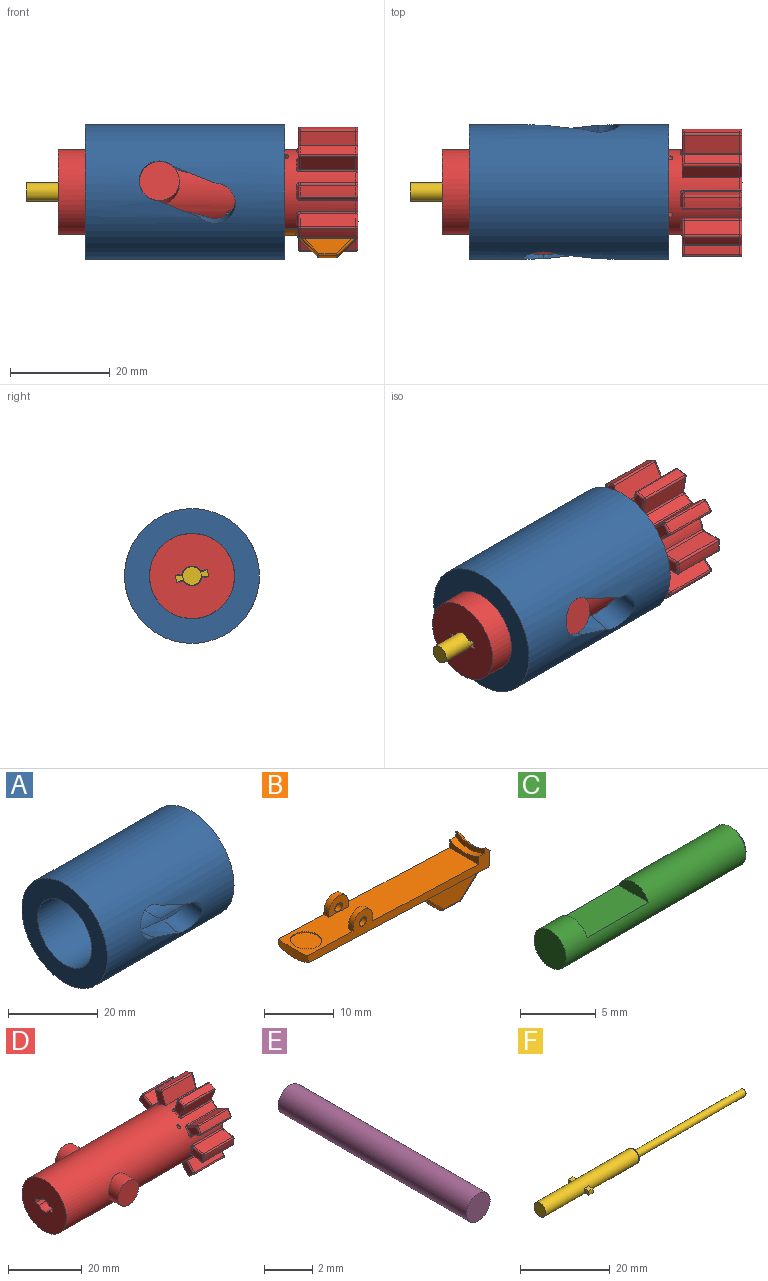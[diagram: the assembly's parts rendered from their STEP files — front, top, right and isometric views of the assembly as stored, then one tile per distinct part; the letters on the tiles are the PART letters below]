
ASSEMBLY  parts=6 mates=5
PART A: 23 faces, bbox 40x44.8x27 mm
  f0: cylinder r=8.55mm len=40mm, axis (-1,0,0), area 1773.2mm2, adj f2,f3,f5,f7,f8,f9,f10,f11
  f1: cylinder r=13.5mm len=40mm, axis (-1,0,0), area 3101mm2, adj f2,f4,f5,f7,f8,f9,f10,f12
  f2: bspline ~15.74x11.11mm, area 48.5mm2, adj f0,f1,f3,f6,f18,f19
  f3: bspline ~11.11x10.63mm, area 0mm2, adj f0,f2,f6,f18
  f4: bspline ~15.67x11.11mm, area 0mm2, adj f1,f18
  f5: bspline ~9.14x6.57mm, area 48.5mm2, adj f0,f1,f18,f19
  f6: plane 2.63x0.46mm, normal (1,0,0), area 0mm2, adj f2,f3,f18
  f7: bspline ~9.3x6.59mm, area 49.3mm2, adj f0,f1,f16,f17
  f8: plane 5.28x0.98mm, normal (1,0,0), area 0.3mm2, adj f0,f1,f11,f12,f15
  f9: plane 27.04x27.04mm, normal (1,0,0), area 339.9mm2, adj f0,f1,f20,f21,f22
  f10: plane 27x27mm, normal (-1,0,0), area 342.9mm2, adj f0,f1
  f11: bspline ~0.48x0.16mm, area 0mm2, adj f0,f8,f12
  f12: bspline ~15.74x11.11mm, area 48.5mm2, adj f0,f1,f8,f11,f17
  f13: bspline ~15.67x11.11mm, area 0.7mm2, adj f0,f1,f14,f16
  f14: plane 5.29x0.95mm, normal (1,0,0), area 0.2mm2, adj f0,f1,f13,f15
  f15: cylinder r=4.05mm len=8.96mm, axis (0,0.99,-0.17), area 65.1mm2, adj f0,f1,f8,f14
  f16: cylinder r=4.05mm len=5.76mm, axis (0,0.99,-0.17), area 12.6mm2, adj f0,f1,f7,f13
  f17: cylinder r=4.1mm len=9.08mm, axis (0,-0.98,-0.17), area 80.3mm2, adj f0,f1,f7,f12
  f18: cylinder r=4.1mm len=9.1mm, axis (0,-0.99,0.17), area 80.3mm2, adj f0,f1,f2,f3,f4,f5,f6
  f19: cylinder r=4.1mm len=9.06mm, axis (0,-0.98,-0.17), area 83.6mm2, adj f0,f1,f2,f5
  f20: plane 12.69x0.49mm, normal (0,1,0), area 3.1mm2, adj f0,f9,f22
  f21: plane 12.69x0.49mm, normal (0,-1,0), area 3.1mm2, adj f0,f9,f22
  f22: cylinder r=8.6mm len=12.71mm, axis (1,0,-0.04), area 79.2mm2, adj f0,f9,f20,f21
PART B: 61 faces, bbox 38.6x8.2x11.3 mm
  f0: plane 37.16x5.21mm, normal (0,-1,0), area 61.9mm2, adj f6,f7,f9,f10,f11,f12,f13,f15
  f1: plane 37.16x5.21mm, normal (0,1,0), area 61.9mm2, adj f4,f5,f6,f7,f10,f11,f12,f13
  f2: plane 4.03x2.88mm, normal (0,-1,0), area 7.7mm2, adj f4,f5,f7,f57,f59
  f3: plane 4.03x2.88mm, normal (0,1,0), area 7.7mm2, adj f7,f52,f53,f56,f58
  f4: plane 0.94x0.8mm, normal (1,0,-0.04), area 0.8mm2, adj f1,f2,f7,f57
  f5: plane 0.94x0.8mm, normal (-1,0,0.04), area 0.8mm2, adj f1,f2,f7,f57
  f6: cylinder r=8.5mm len=36.34mm, axis (1,0,-0.04), area 176.3mm2, adj f0,f1,f9,f17,f22,f23,f26,f27
  f7: plane 36.25x7.2mm, normal (0.04,0,1), area 182.6mm2, adj f0,f1,f2,f3,f4,f5,f51,f52
  f8: plane 11.19x4.13mm, normal (0,1,0), area 28.5mm2, adj f19,f20,f21,f22,f40,f49
  f9: torus R=8.1mm, axis (1,0,-0.04), area 0.8mm2, adj f0,f6,f15,f30
  f10: cone r=5.23mm half-angle=38.1deg, axis (1,0,-0.04), area 7.8mm2, adj f0,f1,f12,f15
  f11: plane 5.9x1.61mm, normal (-1,0,0.04), area 4.4mm2, adj f0,f1,f12,f13
  f12: torus R=5.29mm, axis (1,0,-0.04), area 0.9mm2, adj f0,f1,f10,f11
  f13: cylinder r=6mm len=5.9mm, axis (1,0,-0.04), area 7.2mm2, adj f0,f1,f11,f51
  f14: cylinder r=13mm len=3.55mm, axis (-1,0,0.04), area 7.9mm2, adj f20,f24,f41,f48
  f15: plane 5.91x3.51mm, normal (1,0,-0.04), area 14.4mm2, adj f0,f1,f9,f10,f17,f18,f19,f28
  f16: plane 11.19x4.13mm, normal (0,-1,0), area 28.5mm2, adj f24,f25,f28,f29,f37,f44
  f17: torus R=8.1mm, axis (1,0,-0.04), area 0.8mm2, adj f1,f6,f15,f18
  f18: torus R=0.8mm, axis (1,0,-0.04), area 0.5mm2, adj f15,f17,f19,f22
  f19: cylinder r=0.4mm len=0.4mm, axis (0.04,0,1), area 0mm2, adj f8,f15,f18,f47
  f20: cylinder r=0.4mm len=3.56mm, axis (-1,0,0.04), area 2.1mm2, adj f8,f14,f42,f50
  f21: cylinder r=0.4mm len=0.22mm, axis (-0.04,0,-1), area 0mm2, adj f8,f23,f38
  f22: cylinder r=0.4mm len=11.21mm, axis (1,0,-0.04), area 6.1mm2, adj f6,f8,f18,f23
  f23: bspline ~0.98x0.89mm, area 0.5mm2, adj f6,f21,f22,f26,f36
  f24: cylinder r=0.4mm len=3.56mm, axis (-1,0,0.04), area 2.1mm2, adj f14,f16,f39,f46
  f25: cylinder r=0.4mm len=0.22mm, axis (0.04,0,1), area 0mm2, adj f16,f27,f35
  f26: torus R=8.9mm, axis (1,0,-0.04), area 1.1mm2, adj f6,f23,f27,f34
  f27: bspline ~0.95x0.94mm, area 0.5mm2, adj f6,f25,f26,f29,f33
  f28: cylinder r=0.4mm len=0.4mm, axis (-0.04,0,-1), area 0mm2, adj f15,f16,f30,f43
  f29: cylinder r=0.4mm len=11.21mm, axis (1,0,-0.04), area 6.1mm2, adj f6,f16,f27,f30
  f30: torus R=0.8mm, axis (1,0,-0.04), area 0.5mm2, adj f9,f15,f28,f29
  f31: plane 4.02x3.72mm, normal (0.68,0,-0.73), area 11.7mm2, adj f44,f45,f48,f49
  f32: plane 4.04x3.74mm, normal (-0.73,0,-0.68), area 11.8mm2, adj f33,f34,f36,f37,f40,f41
  f33: bspline ~0.35x0.28mm, area 0.1mm2, adj f27,f32,f34,f35
  f34: bspline ~4.26x0.33mm, area 0.5mm2, adj f26,f32,f33,f36
  f35: sphere r=0.4mm, area 0.1mm2, adj f25,f33,f37
  f36: bspline ~0.37x0.28mm, area 0.1mm2, adj f23,f32,f34,f38
  f37: cylinder r=0.4mm len=4.24mm, axis (0.68,0,-0.73), area 3.4mm2, adj f16,f32,f35,f39
  f38: sphere r=0.4mm, area 0.1mm2, adj f21,f36,f40
  f39: sphere r=0.4mm, area 0.1mm2, adj f24,f37,f41
  f40: cylinder r=0.4mm len=4.24mm, axis (0.68,0,-0.73), area 3.4mm2, adj f8,f32,f38,f42
  f41: bspline ~2.22x0.32mm, area 0.7mm2, adj f14,f32,f39,f42
  f42: sphere r=0.4mm, area 0.1mm2, adj f20,f40,f41
  f43: sphere r=0.4mm, area 0.2mm2, adj f28,f44,f45
  f44: cylinder r=0.4mm len=4.24mm, axis (0.73,0,0.68), area 3.4mm2, adj f16,f31,f43,f46
  f45: cylinder r=0.4mm len=2.15mm, axis (0,1,0), area 0.7mm2, adj f15,f31,f43,f47
  f46: sphere r=0.4mm, area 0.1mm2, adj f24,f44,f48
  f47: sphere r=0.4mm, area 0.1mm2, adj f19,f45,f49
  f48: bspline ~2.22x0.33mm, area 0.7mm2, adj f14,f31,f46,f50
  f49: cylinder r=0.4mm len=4.24mm, axis (0.73,0,0.68), area 3.4mm2, adj f8,f31,f47,f50
  f50: sphere r=0.4mm, area 0.1mm2, adj f20,f48,f49
  f51: plane 5.9x1.37mm, normal (-1,0,0.04), area 5mm2, adj f0,f1,f7,f13
  f52: plane 0.94x0.8mm, normal (1,0,-0.04), area 0.8mm2, adj f0,f3,f7,f56
  f53: plane 0.94x0.8mm, normal (-1,0,0.04), area 0.8mm2, adj f0,f3,f7,f56
  f54: cylinder r=2.25mm len=4.5mm, axis (0.04,0,1), area 2.8mm2, adj f7,f55
  f55: plane 4.5x4.5mm, normal (0.04,0,1), area 15.9mm2, adj f54
  f56: cylinder r=2mm len=4mm, axis (0,-1,0), area 5.9mm2, adj f0,f3,f52,f53
  f57: cylinder r=2mm len=4mm, axis (0,-1,0), area 5.9mm2, adj f1,f2,f4,f5
  f58: cylinder r=0.75mm len=1.5mm, axis (0,-1,0), area 4.4mm2, adj f0,f3
  f59: cylinder r=0.75mm len=1.5mm, axis (0,-1,0), area 4.4mm2, adj f1,f2
  f60: cone r=8.5mm half-angle=76deg, axis (1,0,-0.04), area 8mm2, adj f0,f1,f6,f7
PART C: 7 faces, bbox 17x3x3 mm
  f0: cylinder r=1.5mm len=16.8mm, axis (-1,0,0), area 138.1mm2, adj f2,f3,f4,f5,f6
  f1: plane 2.6x2.6mm, normal (1,0,0), area 5.3mm2, adj f6
  f2: plane 3x3mm, normal (-1,0,0), area 7.1mm2, adj f0
  f3: plane 2.78x0.93mm, normal (-1,0,0), area 1.9mm2, adj f0,f5
  f4: plane 2.78x0.93mm, normal (1,0,0), area 1.9mm2, adj f0,f5
  f5: plane 5.72x2.78mm, normal (0,0,1), area 15.9mm2, adj f0,f3,f4
  f6: cone r=1.3mm half-angle=45deg, axis (-1,0,0), area 2.5mm2, adj f0,f1
PART D: 248 faces, bbox 60.2x26.2x23.6 mm
  f0: cylinder r=8.5mm len=59.6mm, axis (1,0,0), area 2507.3mm2, adj f9,f148,f149,f150,f151,f152,f153,f154
  f1: cylinder r=6mm len=10.96mm, axis (1,0,0), area 25.7mm2, adj f195,f199,f204,f235,f240
  f2: cylinder r=6mm len=10.96mm, axis (1,0,0), area 25.7mm2, adj f196,f200,f204,f235,f238
  f3: plane 1.69x1.67mm, normal (1,0,0), area 1.7mm2, adj f4,f6,f231,f233
  f4: plane 6.5x1.4mm, normal (0,0,-1), area 9.1mm2, adj f3,f6,f9,f221
  f5: cylinder r=2mm len=40mm, axis (-1,0,0), area 455.9mm2, adj f6,f7,f8,f9,f220,f222,f223,f225
  f6: cylinder r=2mm len=6.5mm, axis (-1,0,0), area 11.3mm2, adj f3,f4,f5,f9,f233,f234
  f7: plane 1.69x1.67mm, normal (1,0,0), area 1.7mm2, adj f5,f8,f228,f229
  f8: plane 6.5x1.4mm, normal (0,0,1), area 9.1mm2, adj f5,f7,f9,f224
  f9: plane 17x17mm, normal (-1,0,0), area 210.5mm2, adj f0,f4,f5,f6,f8,f221,f222,f224
  f10: plane 23.4x6.1mm, normal (0,0,-1), area 137.9mm2, adj f11,f201,f203,f204,f206,f208,f209,f218
  f11: plane 3.1x2.8mm, normal (0,-1,0), area 7mm2, adj f10,f206,f210,f215,f216,f218
  f12: cylinder r=0.4mm len=11.2mm, axis (-1,0,0), area 6.7mm2, adj f13,f68,f70,f71
  f13: sphere r=0.4mm, area 0.3mm2, adj f12,f14,f72
  f14: torus R=12.6mm, axis (1,0,0), area 1.4mm2, adj f13,f15,f68,f73
  f15: sphere r=0.4mm, area 0.2mm2, adj f14,f16,f74
  f16: cylinder r=0.4mm len=11.2mm, axis (-1,0,0), area 6.7mm2, adj f15,f68,f69,f75
  f17: cylinder r=0.4mm len=11.2mm, axis (-1,0,0), area 6.7mm2, adj f18,f66,f67,f76
  f18: sphere r=0.4mm, area 0.2mm2, adj f17,f19,f77
  f19: torus R=12.6mm, axis (1,0,0), area 1.4mm2, adj f18,f20,f66,f78
  f20: sphere r=0.4mm, area 0.2mm2, adj f19,f21,f79
  f21: cylinder r=0.4mm len=11.2mm, axis (-1,0,0), area 6.7mm2, adj f20,f65,f66,f80
  f22: cylinder r=0.4mm len=11.2mm, axis (-1,0,0), area 6.7mm2, adj f23,f63,f64,f81
  f23: sphere r=0.4mm, area 0.2mm2, adj f22,f24,f82
  f24: torus R=12.6mm, axis (1,0,0), area 1.4mm2, adj f23,f25,f63,f83
  f25: sphere r=0.4mm, area 0.3mm2, adj f24,f26,f84
  f26: cylinder r=0.4mm len=11.2mm, axis (-1,0,0), area 6.7mm2, adj f25,f62,f63,f85
  f27: cylinder r=0.4mm len=11.2mm, axis (-1,0,0), area 6.7mm2, adj f28,f57,f58,f90
  f28: sphere r=0.4mm, area 0.3mm2, adj f27,f29,f91
  f29: torus R=12.6mm, axis (1,0,0), area 1.4mm2, adj f28,f30,f57,f92
  f30: sphere r=0.4mm, area 0.2mm2, adj f29,f31,f93
  f31: cylinder r=0.4mm len=11.2mm, axis (-1,0,0), area 6.7mm2, adj f30,f56,f57,f94
  f32: cylinder r=0.4mm len=11.2mm, axis (-1,0,0), area 6.7mm2, adj f33,f53,f55,f95
  f33: sphere r=0.4mm, area 0.3mm2, adj f32,f34,f96
  f34: torus R=12.6mm, axis (1,0,0), area 1.4mm2, adj f33,f35,f53,f97
  f35: sphere r=0.4mm, area 0.2mm2, adj f34,f36,f98
  f36: cylinder r=0.4mm len=11.2mm, axis (-1,0,0), area 6.7mm2, adj f35,f53,f54,f99
  f37: cylinder r=0.4mm len=11.2mm, axis (-1,0,0), area 6.7mm2, adj f38,f50,f52,f100
  f38: sphere r=0.4mm, area 0.2mm2, adj f37,f39,f101
  f39: torus R=12.6mm, axis (1,0,0), area 1.4mm2, adj f38,f40,f50,f102
  f40: sphere r=0.4mm, area 0.2mm2, adj f39,f41,f103
  f41: cylinder r=0.4mm len=11.2mm, axis (-1,0,0), area 6.7mm2, adj f40,f50,f51,f104
  f42: cylinder r=0.4mm len=11.2mm, axis (-1,0,0), area 6.7mm2, adj f43,f47,f49,f105
  f43: sphere r=0.4mm, area 0.2mm2, adj f42,f44,f106
  f44: torus R=12.6mm, axis (1,0,0), area 1.4mm2, adj f43,f45,f47,f107
  f45: sphere r=0.4mm, area 0.3mm2, adj f44,f46,f108
  f46: cylinder r=0.4mm len=11.2mm, axis (-1,0,0), area 6.7mm2, adj f45,f47,f48,f109
  f47: cylinder r=13mm len=11.2mm, axis (-1,0,0), area 24.9mm2, adj f42,f44,f46,f112
  f48: sphere r=0.4mm, area 0.2mm2, adj f46,f111,f112
  f49: sphere r=0.4mm, area 0.2mm2, adj f42,f112,f113
  f50: cylinder r=13mm len=11.2mm, axis (-1,0,0), area 24.9mm2, adj f37,f39,f41,f117
  f51: sphere r=0.4mm, area 0.2mm2, adj f41,f116,f117
  f52: sphere r=0.4mm, area 0.2mm2, adj f37,f117,f118
  f53: cylinder r=13mm len=11.2mm, axis (-1,0,0), area 24.9mm2, adj f32,f34,f36,f122
  f54: sphere r=0.4mm, area 0.2mm2, adj f36,f121,f122
  f55: sphere r=0.4mm, area 0.3mm2, adj f32,f122,f123
  f56: sphere r=0.4mm, area 0.2mm2, adj f31,f126,f127
  f57: cylinder r=13mm len=11.2mm, axis (-1,0,0), area 24.9mm2, adj f27,f29,f31,f127
  f58: sphere r=0.4mm, area 0.2mm2, adj f27,f127,f128
  f59: sphere r=0.4mm, area 0.2mm2, adj f89,f130,f131
  f60: cylinder r=13mm len=11.2mm, axis (-1,0,0), area 24.9mm2, adj f86,f88,f89,f131
  f61: sphere r=0.4mm, area 0.2mm2, adj f86,f131,f132
  f62: sphere r=0.4mm, area 0.2mm2, adj f26,f134,f135
  f63: cylinder r=13mm len=11.2mm, axis (-1,0,0), area 24.9mm2, adj f22,f24,f26,f135
  f64: sphere r=0.4mm, area 0.2mm2, adj f22,f135,f136
  f65: sphere r=0.4mm, area 0.2mm2, adj f21,f139,f140
  f66: cylinder r=13mm len=11.2mm, axis (-1,0,0), area 24.9mm2, adj f17,f19,f21,f140
  f67: sphere r=0.4mm, area 0.2mm2, adj f17,f140,f141
  f68: cylinder r=13mm len=11.2mm, axis (-1,0,0), area 24.9mm2, adj f12,f14,f16,f145
  f69: sphere r=0.4mm, area 0.2mm2, adj f16,f144,f145
  f70: sphere r=0.4mm, area 0.3mm2, adj f12,f145,f146
  f71: plane 11.2x2.95mm, normal (0,-0.77,-0.64), area 43.2mm2, adj f12,f72,f146,f148
  f72: cylinder r=0.4mm len=3.21mm, axis (0,-0.64,0.77), area 2.4mm2, adj f13,f71,f73,f149
  f73: plane 4.23x4.04mm, normal (-1,0,0), area 8mm2, adj f14,f72,f74,f150
  f74: cylinder r=0.4mm len=3.21mm, axis (0,0.64,-0.77), area 2.4mm2, adj f15,f73,f75,f151
  f75: plane 11.2x2.95mm, normal (0,0.77,0.64), area 43.2mm2, adj f16,f74,f144,f152
  f76: plane 11.2x3.8mm, normal (0,-0.17,-0.98), area 43.2mm2, adj f17,f77,f141,f154
  f77: cylinder r=0.4mm len=3.86mm, axis (0,-0.98,0.17), area 2.4mm2, adj f18,f76,f78,f155
  f78: plane 4.04x2.76mm, normal (-1,0,0), area 8mm2, adj f19,f77,f79,f156
  f79: cylinder r=0.4mm len=3.86mm, axis (0,0.98,-0.17), area 2.4mm2, adj f20,f78,f80,f157
  f80: plane 11.2x3.8mm, normal (0,0.17,0.98), area 43.2mm2, adj f21,f79,f139,f158
  f81: plane 11.2x3.34mm, normal (0,0.5,-0.87), area 43.2mm2, adj f22,f82,f136,f160
  f82: cylinder r=0.4mm len=3.54mm, axis (0,-0.87,-0.5), area 2.4mm2, adj f23,f81,f83,f161
  f83: plane 4.3x3.72mm, normal (-1,0,0), area 8mm2, adj f24,f82,f84,f162
  f84: cylinder r=0.4mm len=3.54mm, axis (0,0.87,0.5), area 2.4mm2, adj f25,f83,f85,f163
  f85: plane 11.2x3.34mm, normal (0,-0.5,0.87), area 43.2mm2, adj f26,f84,f134,f164
  f86: cylinder r=0.4mm len=11.2mm, axis (-1,0,0), area 6.7mm2, adj f60,f61,f87,f166
  f87: sphere r=0.4mm, area 0.2mm2, adj f86,f88,f167
  f88: torus R=12.6mm, axis (1,0,0), area 1.5mm2, adj f60,f87,f89,f168,f169
  f89: cylinder r=0.4mm len=11.6mm, axis (-1,0,0), area 6.8mm2, adj f59,f60,f88,f169
  f90: plane 11.2x3.62mm, normal (0,0.94,0.34), area 43.2mm2, adj f27,f91,f128,f171
  f91: cylinder r=0.4mm len=3.76mm, axis (0,0.34,-0.94), area 2.4mm2, adj f28,f90,f92,f172
  f92: plane 4.23x3.29mm, normal (-1,0,0), area 8mm2, adj f29,f91,f93,f173
  f93: cylinder r=0.4mm len=3.76mm, axis (0,-0.34,0.94), area 2.4mm2, adj f30,f92,f94,f174
  f94: plane 11.2x3.62mm, normal (0,-0.94,-0.34), area 43.2mm2, adj f31,f93,f126,f175
  f95: plane 11.2x3.34mm, normal (0,0.5,0.87), area 43.2mm2, adj f32,f96,f123,f177
  f96: cylinder r=0.4mm len=3.54mm, axis (0,0.87,-0.5), area 2.4mm2, adj f33,f95,f97,f178
  f97: plane 4.3x3.72mm, normal (-1,0,0), area 8mm2, adj f34,f96,f98,f179
  f98: cylinder r=0.4mm len=3.54mm, axis (0,-0.87,0.5), area 2.4mm2, adj f35,f97,f99,f180
  f99: plane 11.2x3.34mm, normal (0,-0.5,-0.87), area 43.2mm2, adj f36,f98,f121,f181
  f100: plane 11.2x3.8mm, normal (0,-0.17,0.98), area 43.2mm2, adj f37,f101,f118,f183
  f101: cylinder r=0.4mm len=3.86mm, axis (0,0.98,0.17), area 2.4mm2, adj f38,f100,f102,f184
  f102: plane 4.04x2.76mm, normal (-1,0,0), area 8mm2, adj f39,f101,f103,f185
  f103: cylinder r=0.4mm len=3.86mm, axis (0,-0.98,-0.17), area 2.4mm2, adj f40,f102,f104,f186
  f104: plane 11.2x3.8mm, normal (0,0.17,-0.98), area 43.2mm2, adj f41,f103,f116,f187
  f105: plane 11.2x2.95mm, normal (0,-0.77,0.64), area 43.2mm2, adj f42,f106,f113,f189
  f106: cylinder r=0.4mm len=3.21mm, axis (0,0.64,0.77), area 2.4mm2, adj f43,f105,f107,f190
  f107: plane 4.23x4.04mm, normal (-1,0,0), area 8mm2, adj f44,f106,f108,f191
  f108: cylinder r=0.4mm len=3.21mm, axis (0,-0.64,-0.77), area 2.4mm2, adj f45,f107,f109,f192
  f109: plane 11.2x2.95mm, normal (0,0.77,-0.64), area 43.2mm2, adj f46,f108,f111,f193
  f110: torus R=0.8mm, axis (1,0,0), area 0.5mm2, adj f111,f193,f194,f197
  f111: cylinder r=0.4mm len=3.21mm, axis (0,0.64,0.77), area 2.4mm2, adj f48,f109,f110,f197
  f112: torus R=12.6mm, axis (1,0,0), area 1.4mm2, adj f47,f48,f49,f197
  f113: cylinder r=0.4mm len=3.21mm, axis (0,-0.64,-0.77), area 2.4mm2, adj f49,f105,f114,f197
  f114: torus R=0.8mm, axis (1,0,0), area 0.5mm2, adj f113,f188,f189,f197
  f115: torus R=0.8mm, axis (1,0,0), area 0.5mm2, adj f116,f187,f188,f197
  f116: cylinder r=0.4mm len=3.86mm, axis (0,0.98,0.17), area 2.4mm2, adj f51,f104,f115,f197
  f117: torus R=12.6mm, axis (1,0,0), area 1.4mm2, adj f50,f51,f52,f197
  f118: cylinder r=0.4mm len=3.86mm, axis (0,-0.98,-0.17), area 2.4mm2, adj f52,f100,f119,f197
  f119: torus R=0.8mm, axis (1,0,0), area 0.5mm2, adj f118,f182,f183,f197
  f120: torus R=0.8mm, axis (1,0,0), area 0.5mm2, adj f121,f181,f182,f197
  f121: cylinder r=0.4mm len=3.54mm, axis (0,0.87,-0.5), area 2.4mm2, adj f54,f99,f120,f197
  f122: torus R=12.6mm, axis (1,0,0), area 1.4mm2, adj f53,f54,f55,f197
  f123: cylinder r=0.4mm len=3.54mm, axis (0,-0.87,0.5), area 2.4mm2, adj f55,f95,f124,f197
  f124: torus R=0.8mm, axis (1,0,0), area 0.5mm2, adj f123,f176,f177,f197
  f125: torus R=0.8mm, axis (1,0,0), area 0.5mm2, adj f126,f175,f176,f197
  f126: cylinder r=0.4mm len=3.76mm, axis (0,0.34,-0.94), area 2.4mm2, adj f56,f94,f125,f197
  f127: torus R=12.6mm, axis (1,0,0), area 1.4mm2, adj f56,f57,f58,f197
  f128: cylinder r=0.4mm len=3.76mm, axis (0,-0.34,0.94), area 2.4mm2, adj f58,f90,f129,f197
  f129: torus R=0.8mm, axis (1,0,0), area 0.5mm2, adj f128,f170,f171,f197
  f130: cylinder r=0.4mm len=4.39mm, axis (0,-0.34,-0.94), area 2.7mm2, adj f59,f169,f170,f197
  f131: torus R=12.6mm, axis (1,0,0), area 1.4mm2, adj f59,f60,f61,f197
  f132: cylinder r=0.4mm len=4.39mm, axis (0,0.34,0.94), area 2.7mm2, adj f61,f165,f166,f197
  f133: torus R=0.8mm, axis (1,0,0), area 0.5mm2, adj f134,f164,f165,f197
  f134: cylinder r=0.4mm len=3.54mm, axis (0,-0.87,-0.5), area 2.4mm2, adj f62,f85,f133,f197
  f135: torus R=12.6mm, axis (1,0,0), area 1.4mm2, adj f62,f63,f64,f197
  f136: cylinder r=0.4mm len=3.54mm, axis (0,0.87,0.5), area 2.4mm2, adj f64,f81,f137,f197
  f137: torus R=0.8mm, axis (1,0,0), area 0.5mm2, adj f136,f159,f160,f197
  f138: torus R=0.8mm, axis (1,0,0), area 0.5mm2, adj f139,f158,f159,f197
  f139: cylinder r=0.4mm len=3.86mm, axis (0,-0.98,0.17), area 2.4mm2, adj f65,f80,f138,f197
  f140: torus R=12.6mm, axis (1,0,0), area 1.4mm2, adj f65,f66,f67,f197
  f141: cylinder r=0.4mm len=3.86mm, axis (0,0.98,-0.17), area 2.4mm2, adj f67,f76,f142,f197
  f142: torus R=0.8mm, axis (1,0,0), area 0.5mm2, adj f141,f153,f154,f197
  f143: torus R=0.8mm, axis (1,0,0), area 0.5mm2, adj f144,f152,f153,f197
  f144: cylinder r=0.4mm len=3.21mm, axis (0,-0.64,0.77), area 2.4mm2, adj f69,f75,f143,f197
  f145: torus R=12.6mm, axis (1,0,0), area 1.4mm2, adj f68,f69,f70,f197
  f146: cylinder r=0.4mm len=3.21mm, axis (0,0.64,-0.77), area 2.4mm2, adj f70,f71,f147,f197
  f147: torus R=0.8mm, axis (1,0,0), area 0.5mm2, adj f146,f148,f197,f198
  f148: cylinder r=0.4mm len=11.2mm, axis (1,0,0), area 6.1mm2, adj f0,f71,f147,f149
  f149: bspline ~0.97x0.94mm, area 0.5mm2, adj f0,f72,f148,f150
  f150: torus R=8.9mm, axis (1,0,0), area 1.3mm2, adj f0,f73,f149,f151
  f151: bspline ~0.98x0.92mm, area 0.5mm2, adj f0,f74,f150,f152
  f152: cylinder r=0.4mm len=11.2mm, axis (1,0,0), area 6.1mm2, adj f0,f75,f143,f151
  f153: torus R=8.1mm, axis (1,0,0), area 1.4mm2, adj f0,f142,f143,f197
  f154: cylinder r=0.4mm len=11.2mm, axis (1,0,0), area 6.1mm2, adj f0,f76,f142,f155
  f155: bspline ~0.94x0.9mm, area 0.5mm2, adj f0,f77,f154,f156
  f156: torus R=8.9mm, axis (1,0,0), area 1.3mm2, adj f0,f78,f155,f157
  f157: bspline ~0.98x0.9mm, area 0.5mm2, adj f0,f79,f156,f158
  f158: cylinder r=0.4mm len=11.2mm, axis (1,0,0), area 6.1mm2, adj f0,f80,f138,f157
  f159: torus R=8.1mm, axis (1,0,0), area 1.4mm2, adj f0,f137,f138,f197
  f160: cylinder r=0.4mm len=11.2mm, axis (1,0,0), area 6.1mm2, adj f0,f81,f137,f161
  f161: bspline ~0.97x0.94mm, area 0.5mm2, adj f0,f82,f160,f162
  f162: torus R=8.9mm, axis (1,0,0), area 1.3mm2, adj f0,f83,f161,f163
  f163: bspline ~0.98x0.86mm, area 0.5mm2, adj f0,f84,f162,f164
  f164: cylinder r=0.4mm len=11.2mm, axis (1,0,0), area 6.1mm2, adj f0,f85,f133,f163
  f165: torus R=8.1mm, axis (1,0,0), area 1.7mm2, adj f0,f132,f133,f197
  f166: plane 11.2x3.93mm, normal (0,0.94,-0.34), area 46.8mm2, adj f0,f86,f132,f167
  f167: cylinder r=0.4mm len=4.07mm, axis (0,-0.34,-0.94), area 2.6mm2, adj f0,f87,f166,f168
  f168: plane 4.71x3.83mm, normal (-1,0,0), area 10.5mm2, adj f0,f88,f167,f169
  f169: plane 11.6x3.93mm, normal (0,-0.94,0.34), area 48.5mm2, adj f0,f88,f89,f130,f168
  f170: torus R=8.1mm, axis (1,0,0), area 1.7mm2, adj f0,f129,f130,f197
  f171: cylinder r=0.4mm len=11.2mm, axis (1,0,0), area 6.1mm2, adj f0,f90,f129,f172
  f172: bspline ~0.94x0.94mm, area 0.5mm2, adj f0,f91,f171,f173
  f173: torus R=8.9mm, axis (1,0,0), area 1.3mm2, adj f0,f92,f172,f174
  f174: bspline ~0.98x0.79mm, area 0.5mm2, adj f0,f93,f173,f175
  f175: cylinder r=0.4mm len=11.2mm, axis (1,0,0), area 6.1mm2, adj f0,f94,f125,f174
  f176: torus R=8.1mm, axis (1,0,0), area 1.4mm2, adj f0,f124,f125,f197
  f177: cylinder r=0.4mm len=11.2mm, axis (1,0,0), area 6.1mm2, adj f0,f95,f124,f178
  f178: bspline ~0.94x0.88mm, area 0.5mm2, adj f0,f96,f177,f179
  f179: torus R=8.9mm, axis (1,0,0), area 1.3mm2, adj f0,f97,f178,f180
  f180: bspline ~0.98x0.95mm, area 0.5mm2, adj f0,f98,f179,f181
  f181: cylinder r=0.4mm len=11.2mm, axis (1,0,0), area 6.1mm2, adj f0,f99,f120,f180
  f182: torus R=8.1mm, axis (1,0,0), area 1.4mm2, adj f0,f119,f120,f197
  f183: cylinder r=0.4mm len=11.2mm, axis (1,0,0), area 6.1mm2, adj f0,f100,f119,f184
  f184: bspline ~0.95x0.94mm, area 0.5mm2, adj f0,f101,f183,f185
  f185: torus R=8.9mm, axis (1,0,0), area 1.3mm2, adj f0,f102,f184,f186
  f186: bspline ~0.98x0.85mm, area 0.5mm2, adj f0,f103,f185,f187
  f187: cylinder r=0.4mm len=11.2mm, axis (1,0,0), area 6.1mm2, adj f0,f104,f115,f186
  f188: torus R=8.1mm, axis (1,0,0), area 1.4mm2, adj f0,f114,f115,f197
  f189: cylinder r=0.4mm len=11.2mm, axis (1,0,0), area 6.1mm2, adj f0,f105,f114,f190
  f190: bspline ~0.94x0.94mm, area 0.5mm2, adj f0,f106,f189,f191
  f191: torus R=8.9mm, axis (1,0,0), area 1.3mm2, adj f0,f107,f190,f192
  f192: bspline ~0.98x0.95mm, area 0.5mm2, adj f0,f108,f191,f193
  f193: cylinder r=0.4mm len=11.2mm, axis (1,0,0), area 6.1mm2, adj f0,f109,f110,f192
  f194: torus R=8.1mm, axis (1,0,0), area 0.6mm2, adj f0,f110,f197,f199
  f195: extruded ~0.59x0.39mm, area 0.3mm2, adj f1,f199,f241
  f196: extruded ~0.59x0.39mm, area 0.3mm2, adj f2,f200,f238
  f197: plane 25.26x22.64mm, normal (1,0,0), area 139.8mm2, adj f110,f111,f112,f113,f114,f115,f116,f117
  f198: torus R=8.1mm, axis (1,0,0), area 0.6mm2, adj f0,f147,f197,f200
  f199: plane 2.83x2.42mm, normal (0,1,0), area 6.3mm2, adj f0,f1,f194,f195,f197,f203,f204,f241
  f200: plane 2.83x2.42mm, normal (0,-1,0), area 6.3mm2, adj f0,f2,f196,f197,f198,f201,f204,f238
  f201: plane 35x4.23mm, normal (0,-1,0), area 77.7mm2, adj f0,f10,f200,f202,f207,f215
  f202: plane 6.1x4.8mm, normal (1,0,0), area 28.1mm2, adj f0,f201,f203,f215
  f203: plane 35x4.23mm, normal (0,1,0), area 77.7mm2, adj f0,f10,f199,f202,f205,f215,f217
  f204: plane 13.35x12.01mm, normal (1,0,0), area 109.8mm2, adj f1,f2,f10,f199,f200,f219,f235,f236
  f205: plane 4.21x2.81mm, normal (0,1,0), area 8.4mm2, adj f203,f206,f212,f213,f217
  f206: plane 2.8x1.14mm, normal (-1,0,0), area 3.2mm2, adj f10,f11,f205,f213,f215
  f207: plane 4.21x2.81mm, normal (0,-1,0), area 8.4mm2, adj f201,f209,f211,f214
  f208: plane 3.1x2.8mm, normal (0,1,0), area 7mm2, adj f10,f209,f210,f215,f216,f218
  f209: plane 2.8x1.14mm, normal (-1,0,0), area 3.2mm2, adj f10,f207,f208,f214,f215
  f210: cylinder r=0.69mm len=3.82mm, axis (0,1,0), area 16.6mm2, adj f11,f208
  f211: cylinder r=0.69mm len=3.74mm, axis (0,1,0), area 13.6mm2, adj f0,f207
  f212: cylinder r=0.69mm len=3.74mm, axis (0,1,0), area 13.6mm2, adj f0,f205
  f213: plane 2.1x2.1mm, normal (0,1,0), area 0.9mm2, adj f205,f206,f215
  f214: plane 2.12x2.1mm, normal (0,-1,0), area 0.9mm2, adj f207,f209,f215
  f215: plane 13.7x6.1mm, normal (0,0,-1), area 71.7mm2, adj f11,f201,f202,f203,f206,f208,f209,f213
  f216: plane 3.82x1.8mm, normal (-1,0,0), area 6.9mm2, adj f11,f208,f215,f218
  f217: plane 1x0.25mm, normal (0,1,0), area 0.1mm2, adj f203,f205,f215
  f218: cylinder r=1mm len=3.82mm, axis (0,1,0), area 6mm2, adj f10,f11,f208,f216
  f219: cylinder r=0.95mm len=17.65mm, axis (1,0,0), area 105.4mm2, adj f204,f220
  f220: plane 4x4mm, normal (-1,0,0), area 9.7mm2, adj f5,f219
  f221: plane 8x1.5mm, normal (0,1,0), area 12mm2, adj f4,f9,f222,f223,f231
  f222: plane 8x1.4mm, normal (0,0,1), area 11.2mm2, adj f5,f9,f221,f223
  f223: plane 3.94x2.97mm, normal (-1,0,0), area 5.7mm2, adj f5,f221,f222,f231,f232
  f224: plane 8x1.5mm, normal (0,-1,0), area 12mm2, adj f8,f9,f225,f226,f228
  f225: plane 8x1.4mm, normal (0,0,-1), area 11.2mm2, adj f5,f9,f224,f226
  f226: plane 3.94x2.97mm, normal (-1,0,0), area 5.7mm2, adj f5,f224,f225,f227,f228
  f227: plane 3x1.21mm, normal (0,0.87,0.5), area 4.2mm2, adj f5,f226,f228,f230
  f228: cylinder r=3.34mm len=3mm, axis (1,0,0), area 7.5mm2, adj f7,f224,f226,f227,f229,f230
  f229: plane 1.5x1.21mm, normal (0,-0.87,-0.5), area 2.1mm2, adj f5,f7,f228,f230
  f230: plane 2x1.96mm, normal (1,0,0), area 2mm2, adj f5,f227,f228,f229
  f231: cylinder r=3.34mm len=3mm, axis (1,0,0), area 7.5mm2, adj f3,f221,f223,f232,f233,f234
  f232: plane 3x1.21mm, normal (0,-0.87,-0.5), area 4.2mm2, adj f5,f223,f231,f234
  f233: plane 1.5x1.21mm, normal (0,0.87,0.5), area 2.1mm2, adj f3,f6,f231,f234
  f234: plane 2x1.96mm, normal (1,0,0), area 2mm2, adj f6,f231,f232,f233
  f235: cylinder r=1.7mm len=3.14mm, axis (-1,0,0), area 7.4mm2, adj f1,f2,f204,f239
  f236: cylinder r=1.5mm len=20mm, axis (1,0,0), area 186.7mm2, adj f204,f237,f242,f243
  f237: plane 3x3mm, normal (1,0,0), area 7.1mm2, adj f236
  f238: cone r=6mm half-angle=45deg, axis (1,0,0), area 10.4mm2, adj f2,f196,f197,f200,f239
  f239: cone r=2.2mm half-angle=45deg, axis (1,0,0), area 3.1mm2, adj f197,f235,f238,f240
  f240: cone r=6mm half-angle=45deg, axis (1,0,0), area 9.9mm2, adj f1,f197,f239,f241
  f241: bspline ~0.97x0.85mm, area 0.4mm2, adj f195,f197,f199,f240
  f242: cylinder r=0.43mm len=5.96mm, axis (0,-1,0), area 13.2mm2, adj f0,f236
  f243: cylinder r=0.43mm len=5.96mm, axis (0,-1,0), area 13.2mm2, adj f0,f236
  f244: plane 8x8mm, normal (0,1,0), area 50.3mm2, adj f245
  f245: cylinder r=4mm len=8mm, axis (0,1,0), area 113.8mm2, adj f0,f244
  f246: plane 8x8mm, normal (0,-1,0), area 50.3mm2, adj f247
  f247: cylinder r=4mm len=8mm, axis (0,-1,0), area 112.4mm2, adj f0,f246
PART E: 3 faces, bbox 1.4x11x1.4 mm
  f0: cylinder r=0.69mm len=11mm, axis (0,1,0), area 47.7mm2, adj f1,f2
  f1: plane 1.38x1.38mm, normal (0,-1,0), area 1.5mm2, adj f0
  f2: plane 1.38x1.38mm, normal (0,1,0), area 1.5mm2, adj f0
PART F: 17 faces, bbox 64.4x6.5x4 mm
  f0: cylinder r=1.85mm len=29.4mm, axis (1,0,0), area 338.5mm2, adj f5,f6,f7,f9,f10,f11,f13,f14
  f1: revolved ~1.8x1.8mm, area 2.8mm2, adj f2
  f2: cylinder r=0.9mm len=34.28mm, axis (1,0,0), area 193.8mm2, adj f1,f3
  f3: torus R=1.1mm, axis (1,0,0), area 1.9mm2, adj f2,f4
  f4: plane 3.3x3.3mm, normal (1,0,0), area 4.8mm2, adj f3,f5
  f5: torus R=1.65mm, axis (1,0,0), area 3.5mm2, adj f0,f4
  f6: plane 3.7x3.7mm, normal (-1,0,0), area 10.8mm2, adj f0
  f7: plane 1.47x1.12mm, normal (1,0,0), area 1.6mm2, adj f0,f8,f15,f16
  f8: cylinder r=3.23mm len=1.4mm, axis (1,0,0), area 1.6mm2, adj f7,f9,f15,f16
  f9: plane 1.47x1.12mm, normal (-1,0,0), area 1.6mm2, adj f0,f8,f15,f16
  f10: plane 1.47x1.12mm, normal (1,0,0), area 1.6mm2, adj f0,f12,f13,f14
  f11: plane 1.47x1.12mm, normal (-1,0,0), area 1.6mm2, adj f0,f12,f13,f14
  f12: cylinder r=3.23mm len=1.4mm, axis (1,0,0), area 1.6mm2, adj f10,f11,f13,f14
  f13: plane 1.42x1.4mm, normal (0,0,-1), area 2mm2, adj f0,f10,f11,f12
  f14: plane 1.42x1.4mm, normal (0,0,1), area 2mm2, adj f0,f10,f11,f12
  f15: plane 1.42x1.4mm, normal (0,0,1), area 2mm2, adj f0,f7,f8,f9
  f16: plane 1.42x1.4mm, normal (0,0,-1), area 2mm2, adj f0,f7,f8,f9
PLACE A t=(-53.89,25.25,15.68)mm fixed
PLACE B rot(axis=(-0.99,-0.15,0.01),10.6deg) t=(-55.11,34.21,22.29)mm
PLACE C rot(axis=(-1,0,0),10.4deg) t=(-60.76,32.87,14.98)mm
PLACE D rot(axis=(-1,0,0),10.4deg) t=(-53.73,32.87,14.98)mm
PLACE E rot(axis=(-1,0,0),10.4deg) t=(-59.23,30.99,15.33)mm
PLACE F rot(axis=(-1,0,0),10.4deg) t=(-60.05,32.87,14.98)mm
MATE revolute B.f56 <-> E.f0  axis (0,-0.98,0.18) through (-330.21,21.3,-31.54)mm
MATE cylindrical D.f0 <-> A.f0  axis (1,0,0) through (-334.66,25.25,-26.37)mm
MATE slider C.f0 <-> D.f235  axis (1,0,0) through (-306.5,26.18,-21.32)mm
MATE fastened F.f0 <-> D.f0  axis (1,0,0) through (-370.96,25.25,-26.37)mm
MATE fastened E.f0 <-> D.f210  axis (0,0.98,-0.18) through (-330.21,24.2,-32.08)mm
